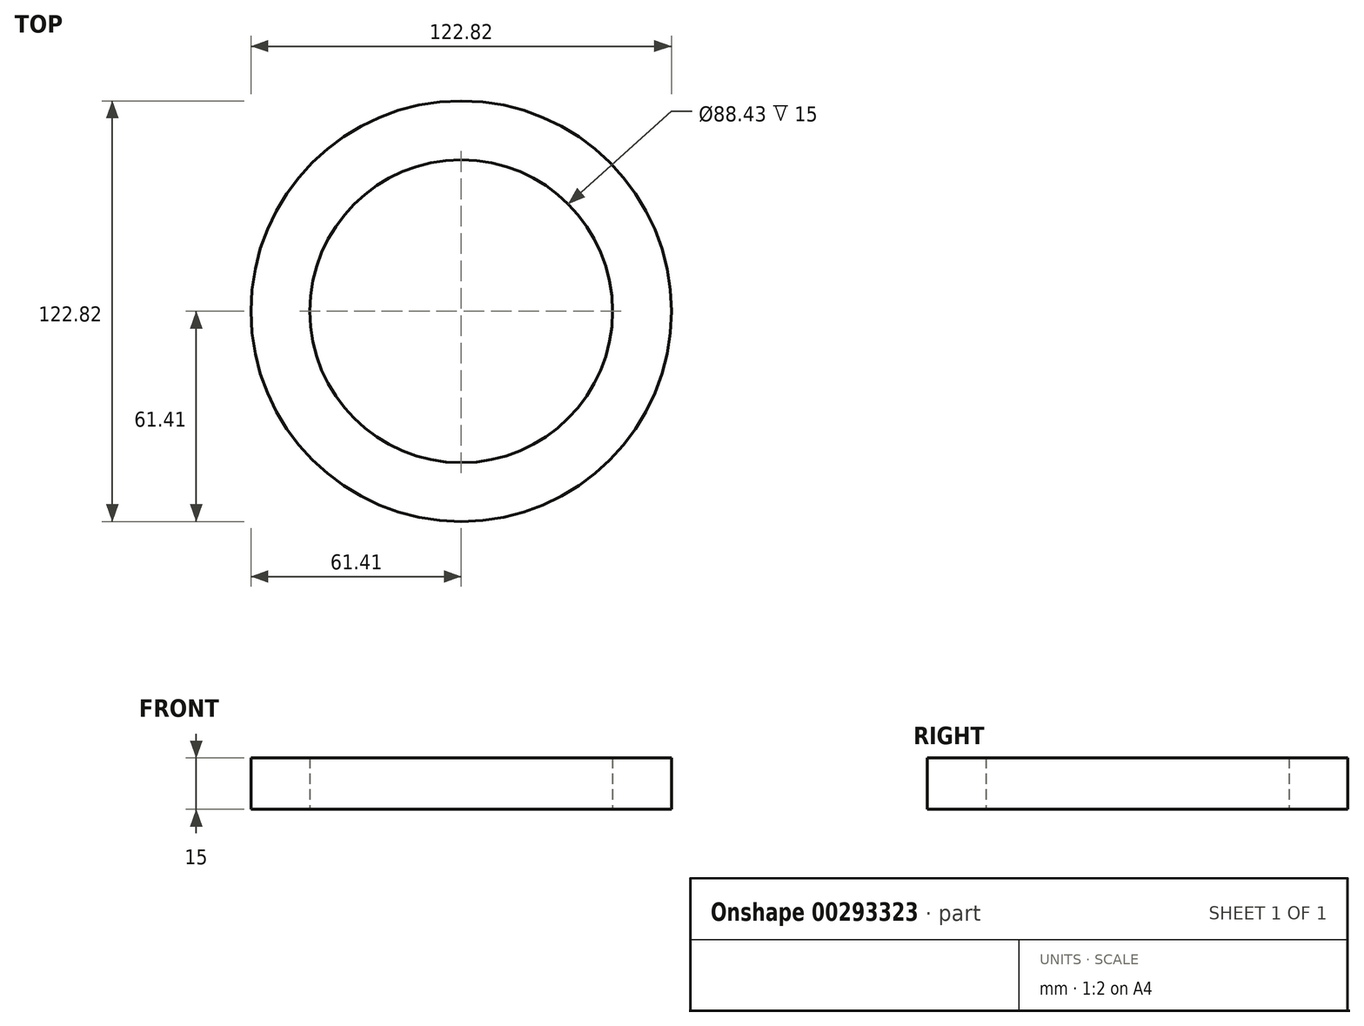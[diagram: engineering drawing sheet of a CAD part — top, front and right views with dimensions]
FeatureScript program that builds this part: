
annotation { "Feature Type Name" : "Feature", "Feature Type Description" : "" }
export const myFeature = defineFeature(function(context is Context, id is Id, definition is map)
    precondition{}
    {
        {
            var Q0;
            Q0=qCreatedBy(makeId("Top.planeOp"),FACE);
            var sketch = newSketch(context, id + "F0", { "sketchPlane" : qUnion([Q0])});
            skCircle(sketch, "E0", {"center": v(0, 0) * mm, "radius": 61.4 * mm});
            skCircle(sketch, "E1", {"center": v(0, 0) * mm, "radius": 44.22 * mm});
            skSolve(sketch);
        }
        {
            var Q0;
            Q0 = qSketchRegion(id + "F0", true);
            extrude(context, id + "F1", {"entities" : qUnion([Q0]), "depth" : 15 * mm});
        }
    });
